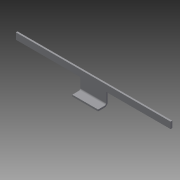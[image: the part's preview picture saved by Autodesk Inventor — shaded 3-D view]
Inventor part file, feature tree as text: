
AUTODESK INVENTOR PART (.ipt)
format: ipt  version: 2013 (Build 170138000, 138)  size: 214,528 bytes
history: native  units: in
note: dims shown in document units (in); Inventor stores cm internally (conversion verified against a paired STEP export)
features: sheet_metal_op x8, other x6, sketch x5, reference x5
ambient origin geometry x8: Origin, YZ Plane, XZ Plane, XY Plane, X Axis, Y Axis, Z Axis, Center Point
bodies: Solid1 (feature_tree)
feature tree (24):
  sheet_metal_op  "Face1"
  sheet_metal_op  "Flange1"
  sheet_metal_op  "Face2"
  sheet_metal_op  "Face3"
  sketch  "Sketch1"  dims[d0=0.5in]
  other  "Plate1"
  sketch  "Sketch2"  dims[d1=2.0in]
  other  "Plate2"
  sheet_metal_op  "Bend1"
  sheet_metal_op  "Corner1"
  sketch  "Sketch3"  dims[d2=0.125in]
  other  "Plate3"
  sheet_metal_op  "Bend2"
  sketch  "Sketch4"  dims[d3=0.125in]
  reference  "Reference1"
  reference  "Reference2"
  reference  "Reference3"
  reference  "Reference4"
  sketch  "Sketch5"  dims[d4=0.0625in d5=0.25in d6=0.125in d7=1.75in d8=90.0deg d9=0.125in d10=0.5in d11=0.125in d12=0.125in d13=2.0in d14=0.5in d15=2.0in d16=0.125in d17=0.125in d18=0.0625in d19=0.25in d20=0.125in d21=0.125in d22=0.0in d23=0.25in d25=0.0625in d27=0.25in d28=0.25in d29=0.0625in d30=0.0625in d31=0.125in d32=0.125in d33=0.0625in d34=0.25in d35=0.125in d36=1.0in d37=0.25in d38=0.0625in]
  reference  "Reference5"
  other  "Plate4"
  sheet_metal_op  "Bend3"
  other  "Cut1"
  other  "Definition1"
